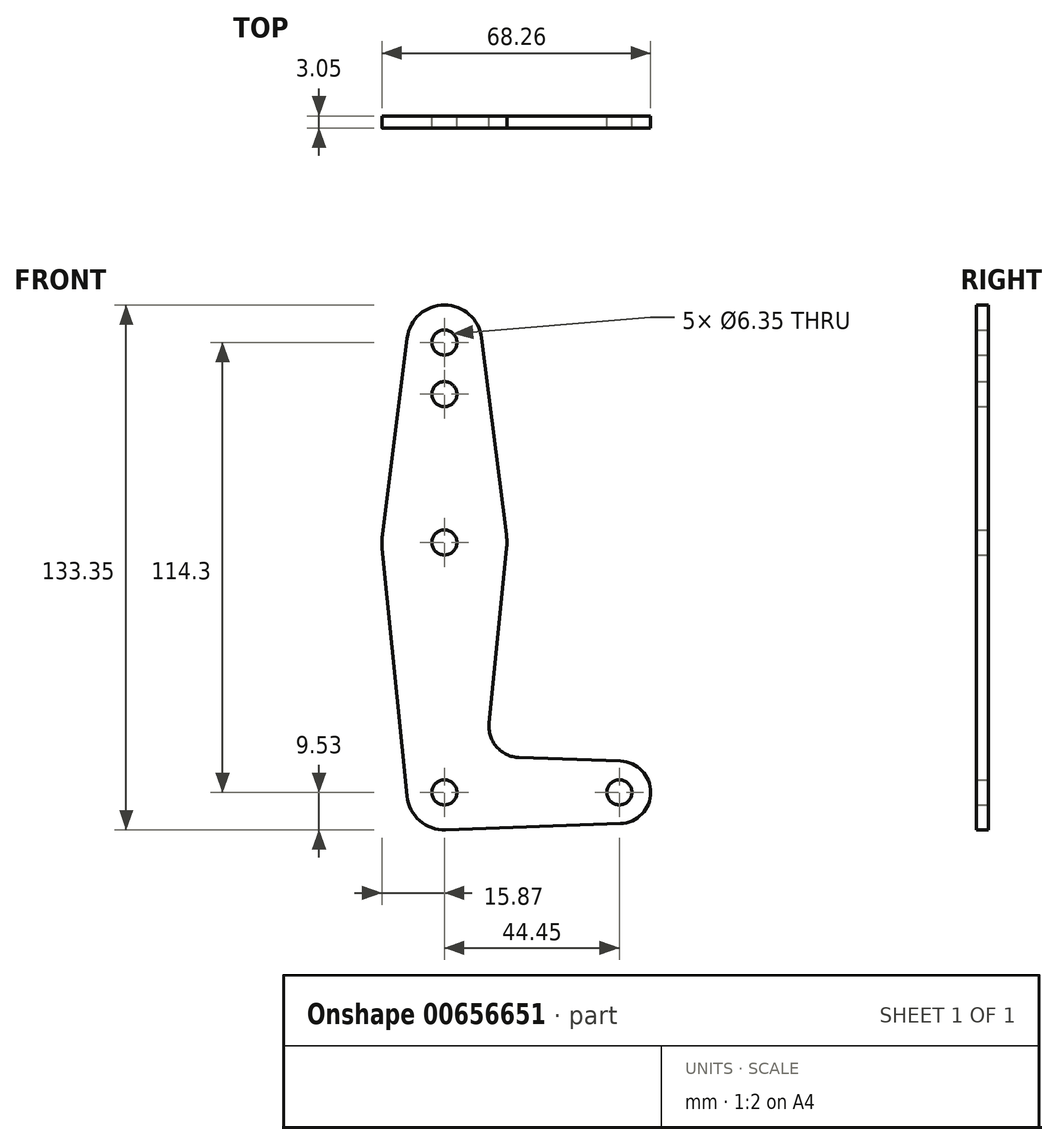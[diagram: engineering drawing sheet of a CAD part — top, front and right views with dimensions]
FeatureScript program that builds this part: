
annotation { "Feature Type Name" : "Feature", "Feature Type Description" : "" }
export const myFeature = defineFeature(function(context is Context, id is Id, definition is map)
    precondition{}
    {
        {
            var Q0;
            Q0=qCreatedBy(makeId("Front.planeOp"),FACE);
            var sketch = newSketch(context, id + "F0", { "sketchPlane" : qUnion([Q0])});
            skCircle(sketch, "E0", {"center": v(0, 50.8) * mm, "radius": 9.53 * mm});
            skCircle(sketch, "E1", {"center": v(0, 0) * mm, "radius": 15.88 * mm});
            skCircle(sketch, "E2", {"center": v(0, -63.5) * mm, "radius": 9.53 * mm});
            skCircle(sketch, "E3", {"center": v(44.45, -63.5) * mm, "radius": 7.94 * mm});
            skLineSegment(sketch, "E4", {"start": v(0, 50.8) * mm, "end": v(0, 0) * mm, "construction": true});
            skLineSegment(sketch, "E5", {"start": v(0, 0) * mm, "end": v(0, -63.5) * mm, "construction": true});
            skLineSegment(sketch, "E6", {"start": v(0, -63.5) * mm, "end": v(44.45, -63.5) * mm, "construction": true});
            skLineSegment(sketch, "E7", {"start": v(-15.8, -1.59) * mm, "end": v(-9.48, -64.45) * mm});
            skLineSegment(sketch, "E8", {"start": v(9.45, 52) * mm, "end": v(15.75, 1.98) * mm});
            skLineSegment(sketch, "E9", {"start": v(44.73, -55.57) * mm, "end": v(18.97, -54.65) * mm});
            skLineSegment(sketch, "E10", {"start": v(44.73, -71.43) * mm, "end": v(0.34, -73.02) * mm});
            skArc(sketch, "E11.filletArc", {"start": v(11.34, -45.9) * mm, "mid": v(13.26, -51.93) * mm, "end": v(18.97, -54.65) * mm});
            skCircle(sketch, "E12", {"center": v(0, 50.8) * mm, "radius": 3.18 * mm});
            skCircle(sketch, "E13", {"center": v(0, 0) * mm, "radius": 3.18 * mm});
            skCircle(sketch, "E14", {"center": v(0, -63.5) * mm, "radius": 3.18 * mm});
            skCircle(sketch, "E15", {"center": v(44.45, -63.5) * mm, "radius": 3.18 * mm});
            skCircle(sketch, "E16", {"center": v(0, 37.67) * mm, "radius": 3.18 * mm});
            skLineSegment(sketch, "E17", {"start": v(15.8, -1.59) * mm, "end": v(11.34, -45.9) * mm});
            skLineSegment(sketch, "E18", {"start": v(-9.45, 52) * mm, "end": v(-15.75, 1.98) * mm});
            skSolve(sketch);
        }
        {
            var Q0;
            Q0 = qSketchRegion(id + "F0", true);
            extrude(context, id + "F1", {"entities" : qUnion([Q0]), "depth" : 3.05 * mm, "offsetDistance" : 25.4 * mm});
        }
    });
